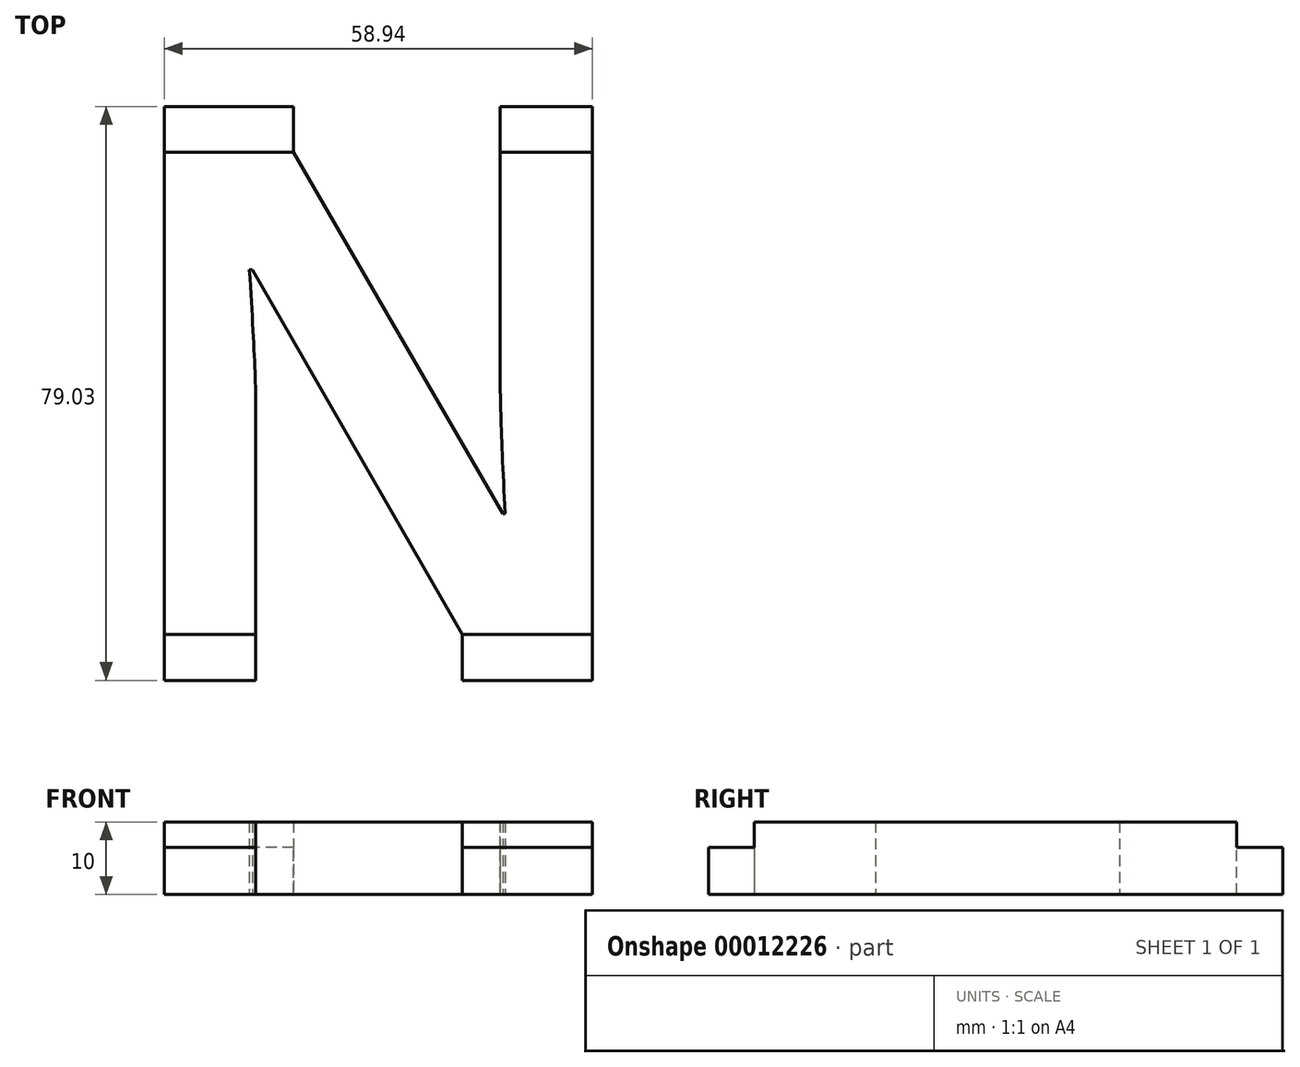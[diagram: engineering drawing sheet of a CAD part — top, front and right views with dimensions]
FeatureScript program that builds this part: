
annotation { "Feature Type Name" : "Feature", "Feature Type Description" : "" }
export const myFeature = defineFeature(function(context is Context, id is Id, definition is map)
    precondition{}
    {
        {
            var Q0;
            Q0=qCreatedBy(makeId("Top.planeOp"),FACE);
            var sketch = newSketch(context, id + "F0", { "sketchPlane" : qUnion([Q0])});
            skText(sketch, "E0", { "text": "N\n", "fontName": "OpenSans-Bold.ttf"});
            const initialGuessF0  = {"E0": [-0.0673, 0, 1, 0, 0.067]};
            skSetInitialGuess(sketch, initialGuessF0);
            skSolve(sketch);
        }
        {
            var Q0;
            Q0=makeQuery(id+"F0.imprint","IMPRINT",FACE,{"disambiguationData":[TD([[makeQuery(id+"F0.imprint","IMPRINT",EDGE,{"derivedFrom":sQuery(id+"F0.wireOp",EDGE,"E0.sketch_text.stroke-0")}),-1.0]])]});
            extrude(context, id + "F1", {"entities" : qUnion([Q0]), "depth" : 10 * mm});
        }
        {
            var Q0;
            Q0=makeQuery(id+"F1.opExtrude","SWEPT_FACE",FACE,{"disambiguationData":[OSD([sQuery(id+"F0.wireOp",EDGE,"E0.sketch_text.stroke-5")])]});
            var sketch = newSketch(context, id + "F2", { "sketchPlane" : qUnion([Q0])});
            skLineSegment(sketch, "E1.1.0", {"start": v(-17.9, 0) * mm, "end": v(0, 0) * mm});
            skLineSegment(sketch, "E1.1.1", {"start": v(0, 0) * mm, "end": v(0, 10) * mm});
            skLineSegment(sketch, "E1.1.2", {"start": v(0, 10) * mm, "end": v(-17.9, 10) * mm});
            skLineSegment(sketch, "E1.1.3", {"start": v(-17.9, 10) * mm, "end": v(-17.9, 0) * mm});
            skLineSegment(sketch, "E2.bottom", {"start": v(-46.34, 0) * mm, "end": v(-58.93, 0) * mm});
            skLineSegment(sketch, "E2.top", {"start": v(-46.34, 6.5) * mm, "end": v(-58.93, 6.5) * mm});
            skLineSegment(sketch, "E2.left", {"start": v(-46.34, 0) * mm, "end": v(-46.34, 6.5) * mm});
            skLineSegment(sketch, "E2.right", {"start": v(-58.93, 0) * mm, "end": v(-58.93, 6.5) * mm});
            skLineSegment(sketch, "E3.top", {"start": v(-17.9, 6.5) * mm, "end": v(0, 6.5) * mm});
            skLineSegment(sketch, "E3.left", {"start": v(-17.9, 0) * mm, "end": v(-17.9, 6.5) * mm});
            skLineSegment(sketch, "E3.right", {"start": v(0, 0) * mm, "end": v(0, 6.5) * mm});
            skSolve(sketch);
        }
        {
            var Q0;
            Q0=makeQuery(id+"F2.imprint","IMPRINT",FACE,{"disambiguationData":[TD([[makeQuery(id+"F2.imprint","IMPRINT",EDGE,{"derivedFrom":sQuery(id+"F2.wireOp",EDGE,"E2.bottom")}),-1.0]])]});
            var Q1;
            Q1=makeQuery(id+"F2.imprint","IMPRINT",FACE,{"disambiguationData":[TD([[makeQuery(id+"F2.imprint","IMPRINT",EDGE,{"derivedFrom":sQuery(id+"F2.wireOp",EDGE,"E1.1.0")}),1.0]])]});
            extrude(context, id + "F3", {"entities" : qUnion([Q0, Q1]), "operationType" : NewBodyOperationType.ADD, "depth" : 6.3 * mm});
        }
        {
            var Q0;
            Q0=makeQuery(id+"F1.opExtrude","SWEPT_FACE",FACE,{"disambiguationData":[OSD([sQuery(id+"F0.wireOp",EDGE,"E0.sketch_text.stroke-12")])]});
            var sketch = newSketch(context, id + "F4", { "sketchPlane" : qUnion([Q0])});
            skLineSegment(sketch, "E4.0.0", {"start": v(0, 0) * mm, "end": v(12.68, 0) * mm});
            skLineSegment(sketch, "E4.0.1", {"start": v(12.68, 0) * mm, "end": v(12.68, 10) * mm});
            skLineSegment(sketch, "E4.0.2", {"start": v(12.68, 10) * mm, "end": v(0, 10) * mm});
            skLineSegment(sketch, "E4.0.3", {"start": v(0, 10) * mm, "end": v(0, 0) * mm});
            skLineSegment(sketch, "E5.0.0", {"start": v(41.16, 0) * mm, "end": v(58.93, 0) * mm});
            skLineSegment(sketch, "E5.0.1", {"start": v(58.93, 0) * mm, "end": v(58.93, 10) * mm});
            skLineSegment(sketch, "E5.0.2", {"start": v(58.93, 10) * mm, "end": v(41.16, 10) * mm});
            skLineSegment(sketch, "E5.0.3", {"start": v(41.16, 10) * mm, "end": v(41.16, 0) * mm});
            skLineSegment(sketch, "E6.top", {"start": v(0, 6.5) * mm, "end": v(12.68, 6.5) * mm});
            skLineSegment(sketch, "E6.left", {"start": v(0, 0) * mm, "end": v(0, 6.5) * mm});
            skLineSegment(sketch, "E6.right", {"start": v(12.68, 0) * mm, "end": v(12.68, 6.5) * mm});
            skLineSegment(sketch, "E7.top", {"start": v(41.16, 6.5) * mm, "end": v(58.93, 6.5) * mm});
            skLineSegment(sketch, "E7.left", {"start": v(41.16, 0) * mm, "end": v(41.16, 6.5) * mm});
            skLineSegment(sketch, "E7.right", {"start": v(58.93, 0) * mm, "end": v(58.93, 6.5) * mm});
            skSolve(sketch);
        }
        {
            var Q0;
            Q0=makeQuery(id+"F4.imprint","IMPRINT",FACE,{"disambiguationData":[TD([[makeQuery(id+"F4.imprint","IMPRINT",EDGE,{"derivedFrom":sQuery(id+"F4.wireOp",EDGE,"E4.0.0")}),-1.0]])]});
            var Q1;
            Q1=makeQuery(id+"F4.imprint","IMPRINT",FACE,{"disambiguationData":[TD([[makeQuery(id+"F4.imprint","IMPRINT",EDGE,{"derivedFrom":sQuery(id+"F4.wireOp",EDGE,"E5.0.0")}),1.0]])]});
            extrude(context, id + "F5", {"entities" : qUnion([Q0, Q1]), "operationType" : NewBodyOperationType.ADD, "depth" : 6.3 * mm});
        }
    });
